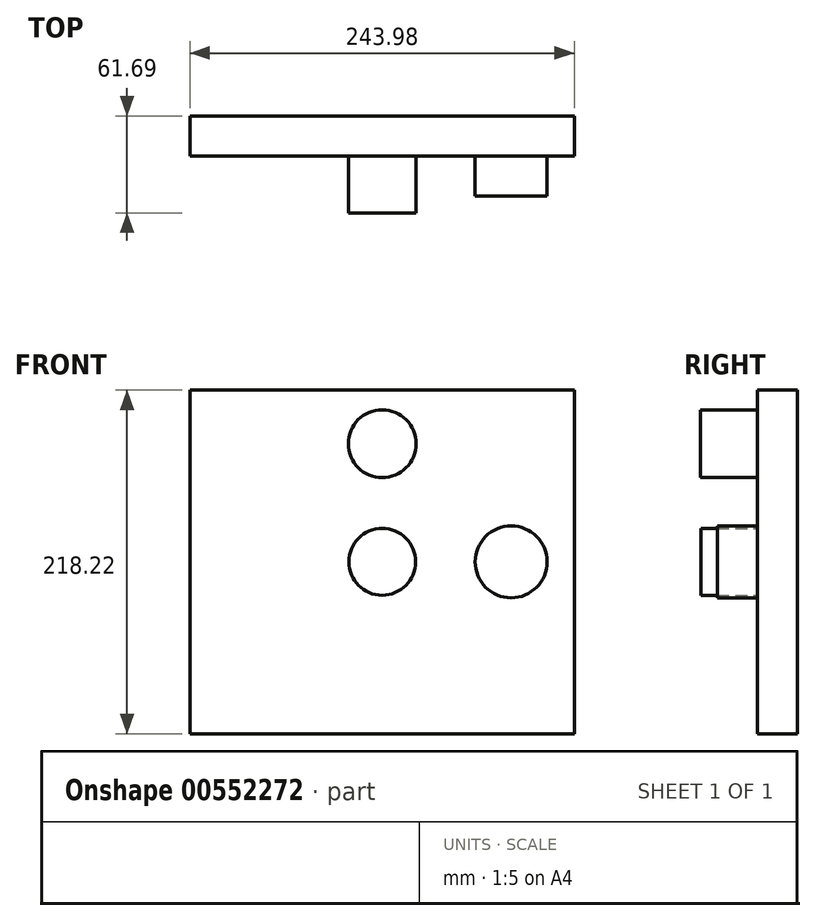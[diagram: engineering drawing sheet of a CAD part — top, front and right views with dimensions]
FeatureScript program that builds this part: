
annotation { "Feature Type Name" : "Feature", "Feature Type Description" : "" }
export const myFeature = defineFeature(function(context is Context, id is Id, definition is map)
    precondition{}
    {
        {
            var Q0;
            Q0=qCreatedBy(makeId("Front.planeOp"),FACE);
            var sketch = newSketch(context, id + "F0", { "sketchPlane" : qUnion([Q0])});
            skLineSegment(sketch, "E0.bottom", {"start": v(122, -109.11) * mm, "end": v(-122, -109.11) * mm});
            skLineSegment(sketch, "E0.top", {"start": v(122, 109.11) * mm, "end": v(-122, 109.11) * mm});
            skLineSegment(sketch, "E0.left", {"start": v(122, -109.11) * mm, "end": v(122, 109.11) * mm});
            skLineSegment(sketch, "E0.right", {"start": v(-122, -109.11) * mm, "end": v(-122, 109.11) * mm});
            skPoint(sketch, "E0.middle", {"position": v(0, 0) * mm});
            skSolve(sketch);
        }
        {
            var Q0;
            Q0=makeQuery(id+"F0.imprint","IMPRINT",FACE,{"disambiguationData":[TD([[makeQuery(id+"F0.imprint","IMPRINT",EDGE,{"derivedFrom":sQuery(id+"F0.wireOp",EDGE,"E0.bottom")}),-1.0]])]});
            extrude(context, id + "F1", {"entities" : qUnion([Q0]), "depth" : 25.4 * mm, "offsetDistance" : 25.4 * mm});
        }
        {
            var Q0;
            Q0=makeQuery(id+"F1.opExtrude","CAP_FACE",FACE,{"disambiguationData":[OSD([sQuery(id+"F0.wireOp",EDGE,"E0.bottom"),sQuery(id+"F0.wireOp",EDGE,"E0.top"),sQuery(id+"F0.wireOp",EDGE,"E0.left"),sQuery(id+"F0.wireOp",EDGE,"E0.right")])],"isStart":false});
            var sketch = newSketch(context, id + "F2", { "sketchPlane" : qUnion([Q0])});
            skCircle(sketch, "E1", {"center": v(0, 0) * mm, "radius": 21.2 * mm});
            skSolve(sketch);
        }
        {
            var Q0;
            Q0=makeQuery(id+"F2.imprint","IMPRINT",FACE,{"disambiguationData":[TD([[makeQuery(id+"F2.imprint","IMPRINT",EDGE,{"derivedFrom":sQuery(id+"F2.wireOp",EDGE,"E1")}),1.0]])]});
            extrude(context, id + "F3", {"entities" : qUnion([Q0]), "operationType" : NewBodyOperationType.ADD, "depth" : 35.96 * mm, "offsetDistance" : 25.4 * mm});
        }
        {
            var Q0;
            Q0=makeQuery(id+"F1.opExtrude","CAP_FACE",FACE,{"disambiguationData":[OSD([sQuery(id+"F0.wireOp",EDGE,"E0.bottom"),sQuery(id+"F0.wireOp",EDGE,"E0.top"),sQuery(id+"F0.wireOp",EDGE,"E0.left"),sQuery(id+"F0.wireOp",EDGE,"E0.right")])],"isStart":false});
            var sketch = newSketch(context, id + "F4", { "sketchPlane" : qUnion([Q0])});
            skCircle(sketch, "E2", {"center": v(0, 75.06) * mm, "radius": 21.53 * mm});
            skSolve(sketch);
        }
        {
            var Q0;
            Q0 = qSketchRegion(id + "F4", true);
            extrude(context, id + "F5", {"entities" : qUnion([Q0]), "operationType" : NewBodyOperationType.ADD, "depth" : 36.3 * mm, "offsetDistance" : 25.4 * mm});
        }
        {
            var Q0;
            Q0=makeQuery(id+"F1.opExtrude","CAP_FACE",FACE,{"disambiguationData":[OSD([sQuery(id+"F0.wireOp",EDGE,"E0.bottom"),sQuery(id+"F0.wireOp",EDGE,"E0.top"),sQuery(id+"F0.wireOp",EDGE,"E0.left"),sQuery(id+"F0.wireOp",EDGE,"E0.right")])],"isStart":false});
            var sketch = newSketch(context, id + "F6", { "sketchPlane" : qUnion([Q0])});
            skCircle(sketch, "E3", {"center": v(81.9, 0) * mm, "radius": 22.84 * mm});
            skSolve(sketch);
        }
        {
            var Q0;
            Q0 = qSketchRegion(id + "F6", true);
            extrude(context, id + "F7", {"entities" : qUnion([Q0]), "operationType" : NewBodyOperationType.ADD, "depth" : 25.4 * mm, "offsetDistance" : 25.4 * mm});
        }
    });
